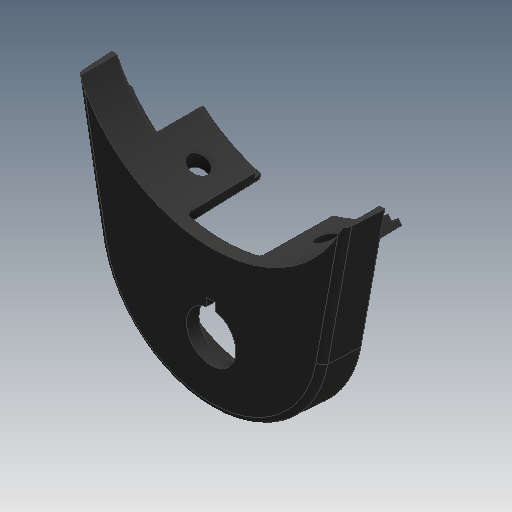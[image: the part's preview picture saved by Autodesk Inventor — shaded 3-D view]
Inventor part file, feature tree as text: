
AUTODESK INVENTOR PART (.ipt)
format: ipt  version: 2019 (Build 230136000, 136)  size: 341,504 bytes
history: native  units: mm
features: fillet x1
ambient origin geometry x8: Origin, YZ Plane, XZ Plane, XY Plane, X Axis, Y Axis, Z Axis, Center Point
bodies: Solid1 (feature_tree)
feature tree (1):
  fillet  "Fillet7"  [1 undecoded]
note: 1 required parameter value undecoded (feature->parameter linkage not recoverable at this tier; creation-order binding heuristic only, values carry confidence <= 0.55)
